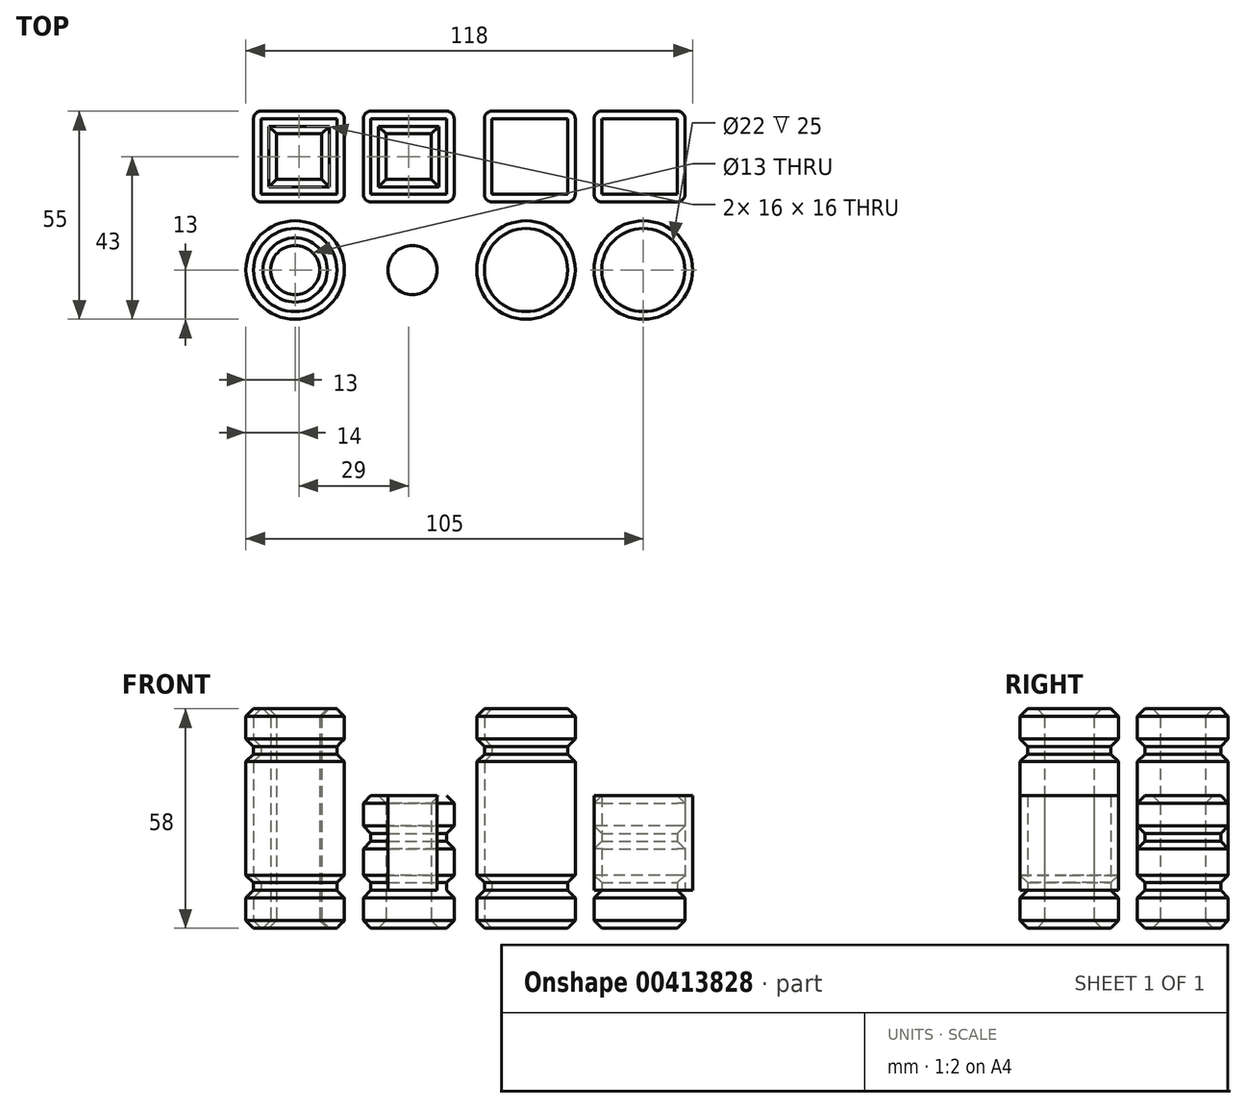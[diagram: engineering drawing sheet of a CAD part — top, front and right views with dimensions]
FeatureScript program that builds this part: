
annotation { "Feature Type Name" : "Feature", "Feature Type Description" : "" }
export const myFeature = defineFeature(function(context is Context, id is Id, definition is map)
    precondition{}
    {
        {
            var Q0;
            Q0=qCreatedBy(makeId("Top.planeOp"),FACE);
            var sketch = newSketch(context, id + "F0", { "sketchPlane" : qUnion([Q0])});
            skCircle(sketch, "E0", {"center": v(-46, -15.5) * mm, "radius": 13 * mm});
            skLineSegment(sketch, "E1.bottom", {"start": v(-35, 2.5) * mm, "end": v(-55, 2.5) * mm});
            skLineSegment(sketch, "E1.top", {"start": v(-35, 26.5) * mm, "end": v(-55, 26.5) * mm});
            skLineSegment(sketch, "E1.left", {"start": v(-33, 4.5) * mm, "end": v(-33, 24.5) * mm});
            skLineSegment(sketch, "E1.right", {"start": v(-57, 4.5) * mm, "end": v(-57, 24.5) * mm});
            skPoint(sketch, "E1.middle", {"position": v(-45, 14.5) * mm});
            skCircle(sketch, "E2.MirrorC", {"center": v(46, -15.5) * mm, "radius": 13 * mm});
            skLineSegment(sketch, "E3.MirrorCS", {"start": v(35, 2.5) * mm, "end": v(55, 2.5) * mm});
            skLineSegment(sketch, "E4.MirrorCS", {"start": v(35, 26.5) * mm, "end": v(55, 26.5) * mm});
            skLineSegment(sketch, "E5.MirrorCS", {"start": v(57, 4.5) * mm, "end": v(57, 24.5) * mm});
            skLineSegment(sketch, "E6.MirrorCS", {"start": v(33, 4.5) * mm, "end": v(33, 24.5) * mm});
            skPoint(sketch, "E7.MirrorP", {"position": v(45, 14.5) * mm});
            skLineSegment(sketch, "E8", {"start": v(-30.5, 50.13) * mm, "end": v(-30.5, -54.87) * mm, "construction": true});
            skLineSegment(sketch, "E9.MirrorCS", {"start": v(30.5, 50.13) * mm, "end": v(30.5, -54.87) * mm, "construction": true});
            skLineSegment(sketch, "E10.MirrorCS", {"start": v(-4, 4.5) * mm, "end": v(-4, 24.5) * mm});
            skLineSegment(sketch, "E11.MirrorCS", {"start": v(-28, 4.5) * mm, "end": v(-28, 24.5) * mm});
            skLineSegment(sketch, "E12.MirrorCS", {"start": v(-26, 26.5) * mm, "end": v(-6, 26.5) * mm});
            skLineSegment(sketch, "E13.MirrorCS", {"start": v(-26, 2.5) * mm, "end": v(-6, 2.5) * mm});
            skPoint(sketch, "E14.MirrorP", {"position": v(-16, 14.5) * mm});
            skCircle(sketch, "E15.MirrorC", {"center": v(-15, -15.5) * mm, "radius": 13 * mm});
            skLineSegment(sketch, "E16.MirrorCS", {"start": v(26, 26.5) * mm, "end": v(6, 26.5) * mm});
            skPoint(sketch, "E17.MirrorP", {"position": v(16, 14.5) * mm});
            skCircle(sketch, "E18.MirrorC", {"center": v(15, -15.5) * mm, "radius": 13 * mm});
            skLineSegment(sketch, "E19.MirrorCS", {"start": v(26, 2.5) * mm, "end": v(6, 2.5) * mm});
            skLineSegment(sketch, "E20.MirrorCS", {"start": v(4, 4.5) * mm, "end": v(4, 24.5) * mm});
            skLineSegment(sketch, "E21.MirrorCS", {"start": v(28, 4.5) * mm, "end": v(28, 24.5) * mm});
            skLineSegment(sketch, "E22.bottom", {"start": v(-39, 8.5) * mm, "end": v(-51, 8.5) * mm});
            skLineSegment(sketch, "E22.top", {"start": v(-39, 20.5) * mm, "end": v(-51, 20.5) * mm});
            skLineSegment(sketch, "E22.left", {"start": v(-39, 8.5) * mm, "end": v(-39, 20.5) * mm});
            skLineSegment(sketch, "E22.right", {"start": v(-51, 8.5) * mm, "end": v(-51, 20.5) * mm});
            skCircle(sketch, "E23", {"center": v(-46, -15.5) * mm, "radius": 6.5 * mm});
            skLineSegment(sketch, "E24.MirrorCS", {"start": v(-22, 20.5) * mm, "end": v(-10, 20.5) * mm});
            skLineSegment(sketch, "E25.MirrorCS", {"start": v(-22, 8.5) * mm, "end": v(-10, 8.5) * mm});
            skLineSegment(sketch, "E26.MirrorCS", {"start": v(-10, 8.5) * mm, "end": v(-10, 20.5) * mm});
            skLineSegment(sketch, "E27.MirrorCS", {"start": v(-22, 8.5) * mm, "end": v(-22, 20.5) * mm});
            skCircle(sketch, "E28.MirrorC", {"center": v(-15, -15.5) * mm, "radius": 6.5 * mm});
            skPoint(sketch, "E29.visualSharp", {"position": v(-57, 26.5) * mm});
            skArc(sketch, "E29.filletArc", {"start": v(-55, 26.5) * mm, "mid": v(-56.41, 25.91) * mm, "end": v(-57, 24.5) * mm});
            skPoint(sketch, "E30.visualSharp", {"position": v(-33, 26.5) * mm});
            skArc(sketch, "E30.filletArc", {"start": v(-33, 24.5) * mm, "mid": v(-33.59, 25.91) * mm, "end": v(-35, 26.5) * mm});
            skPoint(sketch, "E31.visualSharp", {"position": v(-33, 2.5) * mm});
            skArc(sketch, "E31.filletArc", {"start": v(-35, 2.5) * mm, "mid": v(-33.59, 3.09) * mm, "end": v(-33, 4.5) * mm});
            skPoint(sketch, "E32.visualSharp", {"position": v(-57, 2.5) * mm});
            skArc(sketch, "E32.filletArc", {"start": v(-57, 4.5) * mm, "mid": v(-56.41, 3.09) * mm, "end": v(-55, 2.5) * mm});
            skPoint(sketch, "E33.visualSharp", {"position": v(-28, 26.5) * mm});
            skArc(sketch, "E33.filletArc", {"start": v(-26, 26.5) * mm, "mid": v(-27.41, 25.91) * mm, "end": v(-28, 24.5) * mm});
            skPoint(sketch, "E34.visualSharp", {"position": v(-4, 26.5) * mm});
            skArc(sketch, "E34.filletArc", {"start": v(-4, 24.5) * mm, "mid": v(-4.59, 25.91) * mm, "end": v(-6, 26.5) * mm});
            skPoint(sketch, "E35.visualSharp", {"position": v(-4, 2.5) * mm});
            skArc(sketch, "E35.filletArc", {"start": v(-6, 2.5) * mm, "mid": v(-4.59, 3.09) * mm, "end": v(-4, 4.5) * mm});
            skPoint(sketch, "E36.visualSharp", {"position": v(-28, 2.5) * mm});
            skArc(sketch, "E36.filletArc", {"start": v(-28, 4.5) * mm, "mid": v(-27.41, 3.09) * mm, "end": v(-26, 2.5) * mm});
            skPoint(sketch, "E37.visualSharp", {"position": v(4, 26.5) * mm});
            skArc(sketch, "E37.filletArc", {"start": v(6, 26.5) * mm, "mid": v(4.59, 25.91) * mm, "end": v(4, 24.5) * mm});
            skPoint(sketch, "E38.visualSharp", {"position": v(28, 26.5) * mm});
            skArc(sketch, "E38.filletArc", {"start": v(28, 24.5) * mm, "mid": v(27.41, 25.91) * mm, "end": v(26, 26.5) * mm});
            skPoint(sketch, "E39.visualSharp", {"position": v(28, 2.5) * mm});
            skArc(sketch, "E39.filletArc", {"start": v(26, 2.5) * mm, "mid": v(27.41, 3.09) * mm, "end": v(28, 4.5) * mm});
            skPoint(sketch, "E40.visualSharp", {"position": v(4, 2.5) * mm});
            skArc(sketch, "E40.filletArc", {"start": v(4, 4.5) * mm, "mid": v(4.59, 3.09) * mm, "end": v(6, 2.5) * mm});
            skPoint(sketch, "E41.visualSharp", {"position": v(33, 26.5) * mm});
            skArc(sketch, "E41.filletArc", {"start": v(35, 26.5) * mm, "mid": v(33.59, 25.91) * mm, "end": v(33, 24.5) * mm});
            skPoint(sketch, "E42.visualSharp", {"position": v(57, 26.5) * mm});
            skArc(sketch, "E42.filletArc", {"start": v(57, 24.5) * mm, "mid": v(56.41, 25.91) * mm, "end": v(55, 26.5) * mm});
            skPoint(sketch, "E43.visualSharp", {"position": v(57, 2.5) * mm});
            skArc(sketch, "E43.filletArc", {"start": v(55, 2.5) * mm, "mid": v(56.41, 3.09) * mm, "end": v(57, 4.5) * mm});
            skPoint(sketch, "E44.visualSharp", {"position": v(33, 2.5) * mm});
            skArc(sketch, "E44.filletArc", {"start": v(33, 4.5) * mm, "mid": v(33.59, 3.09) * mm, "end": v(35, 2.5) * mm});
            skSolve(sketch);
        }
        {
            var Q0;
            Q0=makeQuery(id+"F0.imprint","IMPRINT",FACE,{"disambiguationData":[TD([[makeQuery(id+"F0.imprint","IMPRINT",EDGE,{"derivedFrom":sQuery(id+"F0.wireOp",EDGE,"E16.MirrorCS")}),1.0]])]});
            var Q1;
            Q1=makeQuery(id+"F0.imprint","IMPRINT",FACE,{"disambiguationData":[TD([[makeQuery(id+"F0.imprint","IMPRINT",EDGE,{"derivedFrom":sQuery(id+"F0.wireOp",EDGE,"E18.MirrorC")}),1.0]])]});
            var Q2;
            Q2=makeQuery(id+"F0.imprint","IMPRINT",FACE,{"disambiguationData":[TD([[makeQuery(id+"F0.imprint","IMPRINT",EDGE,{"derivedFrom":sQuery(id+"F0.wireOp",EDGE,"E0")}),1.0]])]});
            var Q3;
            Q3=makeQuery(id+"F0.imprint","IMPRINT",FACE,{"disambiguationData":[TD([[makeQuery(id+"F0.imprint","IMPRINT",EDGE,{"derivedFrom":sQuery(id+"F0.wireOp",EDGE,"E10.MirrorCS")}),1.0]])]});
            var Q4;
            Q4=makeQuery(id+"F0.imprint","IMPRINT",FACE,{"disambiguationData":[TD([[makeQuery(id+"F0.imprint","IMPRINT",EDGE,{"derivedFrom":sQuery(id+"F0.wireOp",EDGE,"E15.MirrorC")}),-1.0]])]});
            var Q5;
            Q5=makeQuery(id+"F0.imprint","IMPRINT",FACE,{"disambiguationData":[TD([[makeQuery(id+"F0.imprint","IMPRINT",EDGE,{"derivedFrom":sQuery(id+"F0.wireOp",EDGE,"E3.MirrorCS")}),1.0]])]});
            var Q6;
            Q6=makeQuery(id+"F0.imprint","IMPRINT",FACE,{"disambiguationData":[TD([[makeQuery(id+"F0.imprint","IMPRINT",EDGE,{"derivedFrom":sQuery(id+"F0.wireOp",EDGE,"E2.MirrorC")}),-1.0]])]});
            var Q7;
            Q7=makeQuery(id+"F0.imprint","IMPRINT",FACE,{"disambiguationData":[TD([[makeQuery(id+"F0.imprint","IMPRINT",EDGE,{"derivedFrom":sQuery(id+"F0.wireOp",EDGE,"E1.bottom")}),-1.0]])]});
            extrude(context, id + "F1", {"entities" : qUnion([Q0, Q1, Q2, Q3, Q4, Q5, Q6, Q7]), "depth" : 10 * mm});
        }
        {
            var Q0;
            Q0=makeQuery(id+"F1.opExtrude","CAP_FACE",FACE,{"disambiguationData":[OSD([sQuery(id+"F0.wireOp",EDGE,"E18.MirrorC")])],"isStart":false});
            var sketch = newSketch(context, id + "F2", { "sketchPlane" : qUnion([Q0])});
            skCircle(sketch, "E45.0.0", {"center": v(-46, -15.5) * mm, "radius": 13 * mm, "construction": true});
            skCircle(sketch, "E46.0.0", {"center": v(-15, -15.5) * mm, "radius": 13 * mm, "construction": true});
            skCircle(sketch, "E47.0.0", {"center": v(15, -15.5) * mm, "radius": 13 * mm, "construction": true});
            skCircle(sketch, "E48.0.0", {"center": v(46, -15.5) * mm, "radius": 13 * mm, "construction": true});
            skPoint(sketch, "E49.0", {"position": v(-45, 14.5) * mm});
            skPoint(sketch, "E50.0", {"position": v(-16, 14.5) * mm});
            skPoint(sketch, "E51.0", {"position": v(16, 14.5) * mm});
            skPoint(sketch, "E52.0", {"position": v(45, 14.5) * mm});
            skCircle(sketch, "E53.0.0", {"center": v(46, -15.5) * mm, "radius": 13 * mm});
            skLineSegment(sketch, "E54.bottom", {"start": v(-35, 4.5) * mm, "end": v(-55, 4.5) * mm});
            skLineSegment(sketch, "E54.top", {"start": v(-35, 24.5) * mm, "end": v(-55, 24.5) * mm});
            skLineSegment(sketch, "E54.left", {"start": v(-35, 4.5) * mm, "end": v(-35, 24.5) * mm});
            skLineSegment(sketch, "E54.right", {"start": v(-55, 4.5) * mm, "end": v(-55, 24.5) * mm});
            skLineSegment(sketch, "E55.0", {"start": v(-30.5, 50.13) * mm, "end": v(-30.5, -54.87) * mm, "construction": true});
            skLineSegment(sketch, "E56.0", {"start": v(30.5, 50.13) * mm, "end": v(30.5, -54.87) * mm, "construction": true});
            skLineSegment(sketch, "E57.0", {"start": v(-51, 8.5) * mm, "end": v(-51, 20.5) * mm});
            skLineSegment(sketch, "E58.0", {"start": v(-39, 20.5) * mm, "end": v(-51, 20.5) * mm});
            skLineSegment(sketch, "E59.0", {"start": v(-39, 8.5) * mm, "end": v(-39, 20.5) * mm});
            skPoint(sketch, "E60.0", {"position": v(-45, 8.5) * mm});
            skLineSegment(sketch, "E61.0", {"start": v(-39, 8.5) * mm, "end": v(-51, 8.5) * mm});
            skLineSegment(sketch, "E62.0", {"start": v(-22, 8.5) * mm, "end": v(-10, 8.5) * mm});
            skLineSegment(sketch, "E63.0", {"start": v(-22, 8.5) * mm, "end": v(-22, 20.5) * mm});
            skLineSegment(sketch, "E64.0", {"start": v(-22, 20.5) * mm, "end": v(-10, 20.5) * mm});
            skLineSegment(sketch, "E65.0", {"start": v(-10, 8.5) * mm, "end": v(-10, 20.5) * mm});
            skCircle(sketch, "E66.0", {"center": v(-46, -15.5) * mm, "radius": 6.5 * mm});
            skCircle(sketch, "E67.0", {"center": v(-15, -15.5) * mm, "radius": 6.5 * mm});
            skLineSegment(sketch, "E68.MirrorCS", {"start": v(-26, 4.5) * mm, "end": v(-26, 24.5) * mm});
            skLineSegment(sketch, "E69.MirrorCS", {"start": v(-26, 24.5) * mm, "end": v(-6, 24.5) * mm});
            skLineSegment(sketch, "E70.MirrorCS", {"start": v(-6, 4.5) * mm, "end": v(-6, 24.5) * mm});
            skLineSegment(sketch, "E71.MirrorCS", {"start": v(-26, 4.5) * mm, "end": v(-6, 4.5) * mm});
            skCircle(sketch, "E72", {"center": v(-46, -15.5) * mm, "radius": 11 * mm});
            skCircle(sketch, "E73.MirrorC", {"center": v(-15, -15.5) * mm, "radius": 11 * mm});
            skLineSegment(sketch, "E74.MirrorCS", {"start": v(6, 4.5) * mm, "end": v(6, 24.5) * mm});
            skLineSegment(sketch, "E75.MirrorCS", {"start": v(26, 24.5) * mm, "end": v(6, 24.5) * mm});
            skLineSegment(sketch, "E76.MirrorCS", {"start": v(26, 4.5) * mm, "end": v(26, 24.5) * mm});
            skLineSegment(sketch, "E77.MirrorCS", {"start": v(26, 4.5) * mm, "end": v(6, 4.5) * mm});
            skLineSegment(sketch, "E78.MirrorCS", {"start": v(35, 4.5) * mm, "end": v(35, 24.5) * mm});
            skLineSegment(sketch, "E79.MirrorCS", {"start": v(35, 24.5) * mm, "end": v(55, 24.5) * mm});
            skLineSegment(sketch, "E80.MirrorCS", {"start": v(55, 4.5) * mm, "end": v(55, 24.5) * mm});
            skLineSegment(sketch, "E81.MirrorCS", {"start": v(35, 4.5) * mm, "end": v(55, 4.5) * mm});
            skCircle(sketch, "E82.MirrorC", {"center": v(15, -15.5) * mm, "radius": 11 * mm});
            skCircle(sketch, "E83.MirrorC", {"center": v(46, -15.5) * mm, "radius": 11 * mm});
            skSolve(sketch);
        }
        {
            var Q0;
            Q0=makeQuery(id+"F2.imprint","IMPRINT",FACE,{"disambiguationData":[TD([[makeQuery(id+"F2.imprint","IMPRINT",EDGE,{"derivedFrom":sQuery(id+"F2.wireOp",EDGE,"E54.bottom")}),-1.0]])]});
            var Q1;
            Q1=makeQuery(id+"F2.imprint","IMPRINT",FACE,{"disambiguationData":[TD([[makeQuery(id+"F2.imprint","IMPRINT",EDGE,{"derivedFrom":sQuery(id+"F2.wireOp",EDGE,"E66.0")}),-1.0]])]});
            var Q2;
            Q2=makeQuery(id+"F2.imprint","IMPRINT",FACE,{"disambiguationData":[TD([[makeQuery(id+"F2.imprint","IMPRINT",EDGE,{"derivedFrom":sQuery(id+"F2.wireOp",EDGE,"E82.MirrorC")}),1.0]])]});
            var Q3;
            Q3=makeQuery(id+"F2.imprint","IMPRINT",FACE,{"disambiguationData":[TD([[makeQuery(id+"F2.imprint","IMPRINT",EDGE,{"derivedFrom":sQuery(id+"F2.wireOp",EDGE,"E74.MirrorCS")}),-1.0]])]});
            extrude(context, id + "F3", {"entities" : qUnion([Q0, Q1, Q2, Q3]), "operationType" : NewBodyOperationType.ADD, "depth" : 48 * mm});
        }
        {
            var Q0;
            Q0=makeQuery(id+"F2.imprint","IMPRINT",FACE,{"disambiguationData":[TD([[makeQuery(id+"F2.imprint","IMPRINT",EDGE,{"derivedFrom":sQuery(id+"F2.wireOp",EDGE,"E62.0")}),-1.0]])]});
            var Q1;
            Q1=makeQuery(id+"F2.imprint","IMPRINT",FACE,{"disambiguationData":[TD([[makeQuery(id+"F2.imprint","IMPRINT",EDGE,{"derivedFrom":sQuery(id+"F2.wireOp",EDGE,"E67.0")}),1.0]])]});
            var Q2;
            Q2=makeQuery(id+"F2.imprint","IMPRINT",FACE,{"disambiguationData":[TD([[makeQuery(id+"F2.imprint","IMPRINT",EDGE,{"derivedFrom":sQuery(id+"F2.wireOp",EDGE,"E78.MirrorCS")}),-1.0]])]});
            var Q3;
            Q3=makeQuery(id+"F2.imprint","IMPRINT",FACE,{"disambiguationData":[TD([[makeQuery(id+"F2.imprint","IMPRINT",EDGE,{"derivedFrom":sQuery(id+"F2.wireOp",EDGE,"E83.MirrorC")}),-1.0]])]});
            extrude(context, id + "F4", {"entities" : qUnion([Q0, Q1, Q2, Q3]), "operationType" : NewBodyOperationType.ADD, "depth" : 25 * mm});
        }
        {
            var Q0;
            Q0=makeQuery(id+"F0.imprint","IMPRINT",FACE,{"disambiguationData":[TD([[makeQuery(id+"F0.imprint","IMPRINT",EDGE,{"derivedFrom":sQuery(id+"F0.wireOp",EDGE,"E1.bottom")}),-1.0]])]});
            var Q1;
            Q1=makeQuery(id+"F0.imprint","IMPRINT",FACE,{"disambiguationData":[TD([[makeQuery(id+"F0.imprint","IMPRINT",EDGE,{"derivedFrom":sQuery(id+"F0.wireOp",EDGE,"E0")}),1.0]])]});
            var Q2;
            Q2=makeQuery(id+"F0.imprint","IMPRINT",FACE,{"disambiguationData":[TD([[makeQuery(id+"F0.imprint","IMPRINT",EDGE,{"derivedFrom":sQuery(id+"F0.wireOp",EDGE,"E18.MirrorC")}),1.0]])]});
            var Q3;
            Q3=makeQuery(id+"F0.imprint","IMPRINT",FACE,{"disambiguationData":[TD([[makeQuery(id+"F0.imprint","IMPRINT",EDGE,{"derivedFrom":sQuery(id+"F0.wireOp",EDGE,"E16.MirrorCS")}),1.0]])]});
            extrude(context, id + "F5", {"entities" : qUnion([Q0, Q1, Q2, Q3]), "operationType" : NewBodyOperationType.ADD, "depth" : 46 * mm, "hasSecondDirection" : true, "secondDirectionOppositeDirection" : false, "secondDirectionDepth" : 12 * mm});
        }
        {
            var Q0;
            Q0=makeQuery(id+"F0.imprint","IMPRINT",FACE,{"disambiguationData":[TD([[makeQuery(id+"F0.imprint","IMPRINT",EDGE,{"derivedFrom":sQuery(id+"F0.wireOp",EDGE,"E10.MirrorCS")}),1.0]])]});
            var Q1;
            Q1=makeQuery(id+"F0.imprint","IMPRINT",FACE,{"disambiguationData":[TD([[makeQuery(id+"F0.imprint","IMPRINT",EDGE,{"derivedFrom":sQuery(id+"F0.wireOp",EDGE,"E15.MirrorC")}),-1.0]])]});
            var Q2;
            Q2=makeQuery(id+"F0.imprint","IMPRINT",FACE,{"disambiguationData":[TD([[makeQuery(id+"F0.imprint","IMPRINT",EDGE,{"derivedFrom":sQuery(id+"F0.wireOp",EDGE,"E2.MirrorC")}),-1.0]])]});
            var Q3;
            Q3=makeQuery(id+"F0.imprint","IMPRINT",FACE,{"disambiguationData":[TD([[makeQuery(id+"F0.imprint","IMPRINT",EDGE,{"derivedFrom":sQuery(id+"F0.wireOp",EDGE,"E3.MirrorCS")}),1.0]])]});
            extrude(context, id + "F6", {"entities" : qUnion([Q0, Q1, Q2, Q3]), "operationType" : NewBodyOperationType.ADD, "depth" : 23 * mm, "hasSecondDirection" : true, "secondDirectionOppositeDirection" : false, "secondDirectionDepth" : 12 * mm});
        }
        {
            var Q0;
            Q0=makeQuery(id+"F5.opExtrude","CAP_FACE",FACE,{"disambiguationData":[OSD([sQuery(id+"F0.wireOp",EDGE,"E1.bottom"),sQuery(id+"F0.wireOp",EDGE,"E1.top"),sQuery(id+"F0.wireOp",EDGE,"E1.left"),sQuery(id+"F0.wireOp",EDGE,"E1.right"),sQuery(id+"F0.wireOp",EDGE,"E22.bottom"),sQuery(id+"F0.wireOp",EDGE,"E22.top"),sQuery(id+"F0.wireOp",EDGE,"E22.left"),sQuery(id+"F0.wireOp",EDGE,"E22.right")])],"isStart":false});
            var Q1;
            Q1=makeQuery(id+"F5.opExtrude","CAP_FACE",FACE,{"disambiguationData":[OSD([sQuery(id+"F0.wireOp",EDGE,"E0"),sQuery(id+"F0.wireOp",EDGE,"E23")])],"isStart":false});
            var Q2;
            Q2=makeQuery(id+"F6.opExtrude","CAP_FACE",FACE,{"disambiguationData":[OSD([sQuery(id+"F0.wireOp",EDGE,"E10.MirrorCS"),sQuery(id+"F0.wireOp",EDGE,"E11.MirrorCS"),sQuery(id+"F0.wireOp",EDGE,"E12.MirrorCS"),sQuery(id+"F0.wireOp",EDGE,"E13.MirrorCS"),sQuery(id+"F0.wireOp",EDGE,"E24.MirrorCS"),sQuery(id+"F0.wireOp",EDGE,"E25.MirrorCS"),sQuery(id+"F0.wireOp",EDGE,"E26.MirrorCS"),sQuery(id+"F0.wireOp",EDGE,"E27.MirrorCS")])],"isStart":false});
            var Q3;
            Q3=makeQuery(id+"F6.opExtrude","CAP_FACE",FACE,{"disambiguationData":[OSD([sQuery(id+"F0.wireOp",EDGE,"E15.MirrorC"),sQuery(id+"F0.wireOp",EDGE,"E28.MirrorC")])],"isStart":false});
            var Q4;
            Q4=makeQuery(id+"F5.opExtrude","CAP_FACE",FACE,{"disambiguationData":[OSD([sQuery(id+"F0.wireOp",EDGE,"E16.MirrorCS"),sQuery(id+"F0.wireOp",EDGE,"E19.MirrorCS"),sQuery(id+"F0.wireOp",EDGE,"E20.MirrorCS"),sQuery(id+"F0.wireOp",EDGE,"E21.MirrorCS")])],"isStart":false});
            var Q5;
            Q5=makeQuery(id+"F5.opExtrude","CAP_FACE",FACE,{"disambiguationData":[OSD([sQuery(id+"F0.wireOp",EDGE,"E18.MirrorC")])],"isStart":false});
            var Q6;
            Q6=makeQuery(id+"F6.opExtrude","CAP_FACE",FACE,{"disambiguationData":[OSD([sQuery(id+"F0.wireOp",EDGE,"E3.MirrorCS"),sQuery(id+"F0.wireOp",EDGE,"E4.MirrorCS"),sQuery(id+"F0.wireOp",EDGE,"E5.MirrorCS"),sQuery(id+"F0.wireOp",EDGE,"E6.MirrorCS")])],"isStart":false});
            var Q7;
            Q7=makeQuery(id+"F6.opExtrude","CAP_FACE",FACE,{"disambiguationData":[OSD([sQuery(id+"F0.wireOp",EDGE,"E2.MirrorC")])],"isStart":false});
            extrude(context, id + "F7", {"entities" : qUnion([Q0, Q1, Q2, Q3, Q4, Q5, Q6, Q7]), "operationType" : NewBodyOperationType.ADD, "depth" : 12 * mm, "hasSecondDirection" : true, "secondDirectionOppositeDirection" : false, "secondDirectionDepth" : 2 * mm});
        }
        {
            var Q0;
            Q0=makeQuery(id+"F1.opExtrude","CAP_EDGE",EDGE,{"disambiguationData":[OSD([sQuery(id+"F0.wireOp",EDGE,"E1.top")])],"isStart":true});
            var Q1;
            Q1=makeQuery(id+"F1.opExtrude","CAP_EDGE",EDGE,{"disambiguationData":[OSD([sQuery(id+"F0.wireOp",EDGE,"E1.right")])],"isStart":true});
            var Q2;
            Q2=makeQuery(id+"F1.opExtrude","CAP_EDGE",EDGE,{"disambiguationData":[OSD([sQuery(id+"F0.wireOp",EDGE,"E1.bottom")])],"isStart":true});
            var Q3;
            Q3=makeQuery(id+"F1.opExtrude","CAP_EDGE",EDGE,{"disambiguationData":[OSD([sQuery(id+"F0.wireOp",EDGE,"E1.left")])],"isStart":true});
            var Q4;
            Q4=makeQuery(id+"F1.opExtrude","CAP_EDGE",EDGE,{"disambiguationData":[OSD([sQuery(id+"F0.wireOp",EDGE,"E22.left")])],"isStart":true});
            var Q5;
            Q5=makeQuery(id+"F1.opExtrude","CAP_EDGE",EDGE,{"disambiguationData":[OSD([sQuery(id+"F0.wireOp",EDGE,"E22.bottom")])],"isStart":true});
            var Q6;
            Q6=makeQuery(id+"F1.opExtrude","CAP_EDGE",EDGE,{"disambiguationData":[OSD([sQuery(id+"F0.wireOp",EDGE,"E22.right")])],"isStart":true});
            var Q7;
            Q7=makeQuery(id+"F1.opExtrude","CAP_EDGE",EDGE,{"disambiguationData":[OSD([sQuery(id+"F0.wireOp",EDGE,"E22.top")])],"isStart":true});
            var Q8;
            Q8=makeQuery(id+"F1.opExtrude","CAP_EDGE",EDGE,{"disambiguationData":[OSD([sQuery(id+"F0.wireOp",EDGE,"E1.right")])],"isStart":false});
            var Q9;
            Q9=makeQuery(id+"F1.opExtrude","CAP_EDGE",EDGE,{"disambiguationData":[OSD([sQuery(id+"F0.wireOp",EDGE,"E1.top")])],"isStart":false});
            var Q10;
            Q10=makeQuery(id+"F5.opExtrude","CAP_EDGE",EDGE,{"disambiguationData":[OSD([sQuery(id+"F0.wireOp",EDGE,"E1.top")])],"isStart":true});
            var Q11;
            Q11=makeQuery(id+"F5.opExtrude","CAP_EDGE",EDGE,{"disambiguationData":[OSD([sQuery(id+"F0.wireOp",EDGE,"E1.right")])],"isStart":true});
            var Q12;
            Q12=makeQuery(id+"F1.opExtrude","CAP_EDGE",EDGE,{"disambiguationData":[OSD([sQuery(id+"F0.wireOp",EDGE,"E1.bottom")])],"isStart":false});
            var Q13;
            Q13=makeQuery(id+"F5.opExtrude","CAP_EDGE",EDGE,{"disambiguationData":[OSD([sQuery(id+"F0.wireOp",EDGE,"E1.bottom")])],"isStart":true});
            var Q14;
            Q14=makeQuery(id+"F1.opExtrude","CAP_EDGE",EDGE,{"disambiguationData":[OSD([sQuery(id+"F0.wireOp",EDGE,"E1.left")])],"isStart":false});
            var Q15;
            Q15=makeQuery(id+"F5.opExtrude","CAP_EDGE",EDGE,{"disambiguationData":[OSD([sQuery(id+"F0.wireOp",EDGE,"E1.left")])],"isStart":true});
            var Q16;
            Q16=makeQuery(id+"F5.opExtrude","CAP_EDGE",EDGE,{"disambiguationData":[OSD([sQuery(id+"F0.wireOp",EDGE,"E1.right")])],"isStart":false});
            var Q17;
            Q17=makeQuery(id+"F7.opExtrude","CAP_EDGE",EDGE,{"disambiguationData":[OSD([sQuery(id+"F0.wireOp",EDGE,"E1.right")])],"isStart":true});
            var Q18;
            Q18=makeQuery(id+"F5.opExtrude","CAP_EDGE",EDGE,{"disambiguationData":[OSD([sQuery(id+"F0.wireOp",EDGE,"E1.bottom")])],"isStart":false});
            var Q19;
            Q19=makeQuery(id+"F7.opExtrude","CAP_EDGE",EDGE,{"disambiguationData":[OSD([sQuery(id+"F0.wireOp",EDGE,"E1.bottom")])],"isStart":true});
            var Q20;
            Q20=makeQuery(id+"F5.opExtrude","CAP_EDGE",EDGE,{"disambiguationData":[OSD([sQuery(id+"F0.wireOp",EDGE,"E1.top")])],"isStart":false});
            var Q21;
            Q21=makeQuery(id+"F7.opExtrude","CAP_EDGE",EDGE,{"disambiguationData":[OSD([sQuery(id+"F0.wireOp",EDGE,"E1.top")])],"isStart":true});
            var Q22;
            Q22=makeQuery(id+"F5.opExtrude","CAP_EDGE",EDGE,{"disambiguationData":[OSD([sQuery(id+"F0.wireOp",EDGE,"E1.left")])],"isStart":false});
            var Q23;
            Q23=makeQuery(id+"F7.opExtrude","CAP_EDGE",EDGE,{"disambiguationData":[OSD([sQuery(id+"F0.wireOp",EDGE,"E1.left")])],"isStart":true});
            var Q24;
            Q24=makeQuery(id+"F7.boolean.opBoolean","MERGE",FACE,{"derivedFrom":[makeQuery(id+"F3.opExtrude","CAP_FACE",FACE,{"disambiguationData":[OSD([sQuery(id+"F2.wireOp",EDGE,"E54.bottom"),sQuery(id+"F2.wireOp",EDGE,"E54.top"),sQuery(id+"F2.wireOp",EDGE,"E54.left"),sQuery(id+"F2.wireOp",EDGE,"E54.right"),sQuery(id+"F2.wireOp",EDGE,"E57.0"),sQuery(id+"F2.wireOp",EDGE,"E58.0"),sQuery(id+"F2.wireOp",EDGE,"E59.0"),sQuery(id+"F2.wireOp",EDGE,"E61.0")])],"isStart":false}),makeQuery(id+"F7.opExtrude","CAP_FACE",FACE,{"disambiguationData":[OSD([sQuery(id+"F0.wireOp",EDGE,"E1.bottom"),sQuery(id+"F0.wireOp",EDGE,"E1.top"),sQuery(id+"F0.wireOp",EDGE,"E1.left"),sQuery(id+"F0.wireOp",EDGE,"E1.right"),sQuery(id+"F0.wireOp",EDGE,"E22.bottom"),sQuery(id+"F0.wireOp",EDGE,"E22.top"),sQuery(id+"F0.wireOp",EDGE,"E22.left"),sQuery(id+"F0.wireOp",EDGE,"E22.right")])],"isStart":false})]});
            var Q25;
            Q25=makeQuery(id+"F1.opExtrude","CAP_FACE",FACE,{"disambiguationData":[OSD([sQuery(id+"F0.wireOp",EDGE,"E0"),sQuery(id+"F0.wireOp",EDGE,"E23")])],"isStart":true});
            var Q26;
            Q26=makeQuery(id+"F1.opExtrude","CAP_EDGE",EDGE,{"disambiguationData":[OSD([sQuery(id+"F0.wireOp",EDGE,"E0")])],"isStart":false});
            var Q27;
            Q27=makeQuery(id+"F5.opExtrude","CAP_EDGE",EDGE,{"disambiguationData":[OSD([sQuery(id+"F0.wireOp",EDGE,"E0")])],"isStart":true});
            var Q28;
            Q28=makeQuery(id+"F5.opExtrude","CAP_EDGE",EDGE,{"disambiguationData":[OSD([sQuery(id+"F0.wireOp",EDGE,"E0")])],"isStart":false});
            var Q29;
            Q29=makeQuery(id+"F7.opExtrude","CAP_EDGE",EDGE,{"disambiguationData":[OSD([sQuery(id+"F0.wireOp",EDGE,"E0")])],"isStart":true});
            var Q30;
            Q30=makeQuery(id+"F7.boolean.opBoolean","MERGE",FACE,{"derivedFrom":[makeQuery(id+"F3.opExtrude","CAP_FACE",FACE,{"disambiguationData":[OSD([sQuery(id+"F2.wireOp",EDGE,"E66.0"),sQuery(id+"F2.wireOp",EDGE,"E72")])],"isStart":false}),makeQuery(id+"F7.opExtrude","CAP_FACE",FACE,{"disambiguationData":[OSD([sQuery(id+"F0.wireOp",EDGE,"E0"),sQuery(id+"F0.wireOp",EDGE,"E23")])],"isStart":false})]});
            var Q31;
            Q31=makeQuery(id+"F1.opExtrude","CAP_FACE",FACE,{"disambiguationData":[OSD([sQuery(id+"F0.wireOp",EDGE,"E10.MirrorCS"),sQuery(id+"F0.wireOp",EDGE,"E11.MirrorCS"),sQuery(id+"F0.wireOp",EDGE,"E12.MirrorCS"),sQuery(id+"F0.wireOp",EDGE,"E13.MirrorCS"),sQuery(id+"F0.wireOp",EDGE,"E24.MirrorCS"),sQuery(id+"F0.wireOp",EDGE,"E25.MirrorCS"),sQuery(id+"F0.wireOp",EDGE,"E26.MirrorCS"),sQuery(id+"F0.wireOp",EDGE,"E27.MirrorCS")])],"isStart":true});
            var Q32;
            Q32=makeQuery(id+"F1.opExtrude","CAP_EDGE",EDGE,{"disambiguationData":[OSD([sQuery(id+"F0.wireOp",EDGE,"E13.MirrorCS")])],"isStart":false});
            var Q33;
            Q33=makeQuery(id+"F6.opExtrude","CAP_EDGE",EDGE,{"disambiguationData":[OSD([sQuery(id+"F0.wireOp",EDGE,"E13.MirrorCS")])],"isStart":true});
            var Q34;
            Q34=makeQuery(id+"F1.opExtrude","CAP_EDGE",EDGE,{"disambiguationData":[OSD([sQuery(id+"F0.wireOp",EDGE,"E11.MirrorCS")])],"isStart":false});
            var Q35;
            Q35=makeQuery(id+"F6.opExtrude","CAP_EDGE",EDGE,{"disambiguationData":[OSD([sQuery(id+"F0.wireOp",EDGE,"E11.MirrorCS")])],"isStart":true});
            var Q36;
            Q36=makeQuery(id+"F6.opExtrude","CAP_EDGE",EDGE,{"disambiguationData":[OSD([sQuery(id+"F0.wireOp",EDGE,"E10.MirrorCS")])],"isStart":true});
            var Q37;
            Q37=makeQuery(id+"F1.opExtrude","CAP_EDGE",EDGE,{"disambiguationData":[OSD([sQuery(id+"F0.wireOp",EDGE,"E10.MirrorCS")])],"isStart":false});
            var Q38;
            Q38=makeQuery(id+"F6.opExtrude","CAP_EDGE",EDGE,{"disambiguationData":[OSD([sQuery(id+"F0.wireOp",EDGE,"E12.MirrorCS")])],"isStart":true});
            var Q39;
            Q39=makeQuery(id+"F1.opExtrude","CAP_EDGE",EDGE,{"disambiguationData":[OSD([sQuery(id+"F0.wireOp",EDGE,"E12.MirrorCS")])],"isStart":false});
            var Q40;
            Q40=makeQuery(id+"F6.opExtrude","CAP_EDGE",EDGE,{"disambiguationData":[OSD([sQuery(id+"F0.wireOp",EDGE,"E12.MirrorCS")])],"isStart":false});
            var Q41;
            Q41=makeQuery(id+"F7.opExtrude","CAP_EDGE",EDGE,{"disambiguationData":[OSD([sQuery(id+"F0.wireOp",EDGE,"E12.MirrorCS")])],"isStart":true});
            var Q42;
            Q42=makeQuery(id+"F7.opExtrude","CAP_EDGE",EDGE,{"disambiguationData":[OSD([sQuery(id+"F0.wireOp",EDGE,"E10.MirrorCS")])],"isStart":true});
            var Q43;
            Q43=makeQuery(id+"F6.opExtrude","CAP_EDGE",EDGE,{"disambiguationData":[OSD([sQuery(id+"F0.wireOp",EDGE,"E10.MirrorCS")])],"isStart":false});
            var Q44;
            Q44=makeQuery(id+"F7.opExtrude","CAP_EDGE",EDGE,{"disambiguationData":[OSD([sQuery(id+"F0.wireOp",EDGE,"E13.MirrorCS")])],"isStart":true});
            var Q45;
            Q45=makeQuery(id+"F6.opExtrude","CAP_EDGE",EDGE,{"disambiguationData":[OSD([sQuery(id+"F0.wireOp",EDGE,"E13.MirrorCS")])],"isStart":false});
            var Q46;
            Q46=makeQuery(id+"F7.opExtrude","CAP_EDGE",EDGE,{"disambiguationData":[OSD([sQuery(id+"F0.wireOp",EDGE,"E11.MirrorCS")])],"isStart":true});
            var Q47;
            Q47=makeQuery(id+"F6.opExtrude","CAP_EDGE",EDGE,{"disambiguationData":[OSD([sQuery(id+"F0.wireOp",EDGE,"E11.MirrorCS")])],"isStart":false});
            var Q48;
            Q48=makeQuery(id+"F7.boolean.opBoolean","MERGE",FACE,{"derivedFrom":[makeQuery(id+"F4.opExtrude","CAP_FACE",FACE,{"disambiguationData":[OSD([sQuery(id+"F2.wireOp",EDGE,"E62.0"),sQuery(id+"F2.wireOp",EDGE,"E63.0"),sQuery(id+"F2.wireOp",EDGE,"E64.0"),sQuery(id+"F2.wireOp",EDGE,"E65.0"),sQuery(id+"F2.wireOp",EDGE,"E68.MirrorCS"),sQuery(id+"F2.wireOp",EDGE,"E69.MirrorCS"),sQuery(id+"F2.wireOp",EDGE,"E70.MirrorCS"),sQuery(id+"F2.wireOp",EDGE,"E71.MirrorCS")])],"isStart":false}),makeQuery(id+"F7.opExtrude","CAP_FACE",FACE,{"disambiguationData":[OSD([sQuery(id+"F0.wireOp",EDGE,"E10.MirrorCS"),sQuery(id+"F0.wireOp",EDGE,"E11.MirrorCS"),sQuery(id+"F0.wireOp",EDGE,"E12.MirrorCS"),sQuery(id+"F0.wireOp",EDGE,"E13.MirrorCS"),sQuery(id+"F0.wireOp",EDGE,"E24.MirrorCS"),sQuery(id+"F0.wireOp",EDGE,"E25.MirrorCS"),sQuery(id+"F0.wireOp",EDGE,"E26.MirrorCS"),sQuery(id+"F0.wireOp",EDGE,"E27.MirrorCS")])],"isStart":false})]});
            var Q49;
            Q49=makeQuery(id+"F1.opExtrude","CAP_FACE",FACE,{"disambiguationData":[OSD([sQuery(id+"F0.wireOp",EDGE,"E15.MirrorC"),sQuery(id+"F0.wireOp",EDGE,"E28.MirrorC")])],"isStart":true});
            var Q50;
            Q50=makeQuery(id+"F1.opExtrude","CAP_EDGE",EDGE,{"disambiguationData":[OSD([sQuery(id+"F0.wireOp",EDGE,"E15.MirrorC")])],"isStart":false});
            var Q51;
            Q51=makeQuery(id+"F6.opExtrude","CAP_EDGE",EDGE,{"disambiguationData":[OSD([sQuery(id+"F0.wireOp",EDGE,"E15.MirrorC")])],"isStart":true});
            var Q52;
            Q52=makeQuery(id+"F6.opExtrude","CAP_EDGE",EDGE,{"disambiguationData":[OSD([sQuery(id+"F0.wireOp",EDGE,"E15.MirrorC")])],"isStart":false});
            var Q53;
            Q53=makeQuery(id+"F7.opExtrude","CAP_EDGE",EDGE,{"disambiguationData":[OSD([sQuery(id+"F0.wireOp",EDGE,"E15.MirrorC")])],"isStart":true});
            var Q54;
            Q54=makeQuery(id+"F7.boolean.opBoolean","MERGE",FACE,{"derivedFrom":[makeQuery(id+"F4.opExtrude","CAP_FACE",FACE,{"disambiguationData":[OSD([sQuery(id+"F2.wireOp",EDGE,"E67.0"),sQuery(id+"F2.wireOp",EDGE,"E73.MirrorC")])],"isStart":false}),makeQuery(id+"F7.opExtrude","CAP_FACE",FACE,{"disambiguationData":[OSD([sQuery(id+"F0.wireOp",EDGE,"E15.MirrorC"),sQuery(id+"F0.wireOp",EDGE,"E28.MirrorC")])],"isStart":false})]});
            var Q55;
            Q55=makeQuery(id+"F1.opExtrude","CAP_FACE",FACE,{"disambiguationData":[OSD([sQuery(id+"F0.wireOp",EDGE,"E16.MirrorCS"),sQuery(id+"F0.wireOp",EDGE,"E19.MirrorCS"),sQuery(id+"F0.wireOp",EDGE,"E20.MirrorCS"),sQuery(id+"F0.wireOp",EDGE,"E21.MirrorCS")])],"isStart":true});
            var Q56;
            Q56=makeQuery(id+"F1.opExtrude","CAP_EDGE",EDGE,{"disambiguationData":[OSD([sQuery(id+"F0.wireOp",EDGE,"E16.MirrorCS")])],"isStart":false});
            var Q57;
            Q57=makeQuery(id+"F1.opExtrude","CAP_EDGE",EDGE,{"disambiguationData":[OSD([sQuery(id+"F0.wireOp",EDGE,"E21.MirrorCS")])],"isStart":false});
            var Q58;
            Q58=makeQuery(id+"F5.opExtrude","CAP_EDGE",EDGE,{"disambiguationData":[OSD([sQuery(id+"F0.wireOp",EDGE,"E16.MirrorCS")])],"isStart":true});
            var Q59;
            Q59=makeQuery(id+"F5.opExtrude","CAP_EDGE",EDGE,{"disambiguationData":[OSD([sQuery(id+"F0.wireOp",EDGE,"E21.MirrorCS")])],"isStart":true});
            var Q60;
            Q60=makeQuery(id+"F1.opExtrude","CAP_EDGE",EDGE,{"disambiguationData":[OSD([sQuery(id+"F0.wireOp",EDGE,"E20.MirrorCS")])],"isStart":false});
            var Q61;
            Q61=makeQuery(id+"F5.opExtrude","CAP_EDGE",EDGE,{"disambiguationData":[OSD([sQuery(id+"F0.wireOp",EDGE,"E20.MirrorCS")])],"isStart":true});
            var Q62;
            Q62=makeQuery(id+"F1.opExtrude","CAP_EDGE",EDGE,{"disambiguationData":[OSD([sQuery(id+"F0.wireOp",EDGE,"E19.MirrorCS")])],"isStart":false});
            var Q63;
            Q63=makeQuery(id+"F5.opExtrude","CAP_EDGE",EDGE,{"disambiguationData":[OSD([sQuery(id+"F0.wireOp",EDGE,"E19.MirrorCS")])],"isStart":true});
            var Q64;
            Q64=makeQuery(id+"F5.opExtrude","CAP_EDGE",EDGE,{"disambiguationData":[OSD([sQuery(id+"F0.wireOp",EDGE,"E20.MirrorCS")])],"isStart":false});
            var Q65;
            Q65=makeQuery(id+"F7.opExtrude","CAP_EDGE",EDGE,{"disambiguationData":[OSD([sQuery(id+"F0.wireOp",EDGE,"E20.MirrorCS")])],"isStart":true});
            var Q66;
            Q66=makeQuery(id+"F7.opExtrude","CAP_EDGE",EDGE,{"disambiguationData":[OSD([sQuery(id+"F0.wireOp",EDGE,"E19.MirrorCS")])],"isStart":true});
            var Q67;
            Q67=makeQuery(id+"F5.opExtrude","CAP_EDGE",EDGE,{"disambiguationData":[OSD([sQuery(id+"F0.wireOp",EDGE,"E19.MirrorCS")])],"isStart":false});
            var Q68;
            Q68=makeQuery(id+"F5.opExtrude","CAP_EDGE",EDGE,{"disambiguationData":[OSD([sQuery(id+"F0.wireOp",EDGE,"E16.MirrorCS")])],"isStart":false});
            var Q69;
            Q69=makeQuery(id+"F7.opExtrude","CAP_EDGE",EDGE,{"disambiguationData":[OSD([sQuery(id+"F0.wireOp",EDGE,"E16.MirrorCS")])],"isStart":true});
            var Q70;
            Q70=makeQuery(id+"F5.opExtrude","CAP_EDGE",EDGE,{"disambiguationData":[OSD([sQuery(id+"F0.wireOp",EDGE,"E21.MirrorCS")])],"isStart":false});
            var Q71;
            Q71=makeQuery(id+"F7.opExtrude","CAP_EDGE",EDGE,{"disambiguationData":[OSD([sQuery(id+"F0.wireOp",EDGE,"E21.MirrorCS")])],"isStart":true});
            var Q72;
            Q72=makeQuery(id+"F7.boolean.opBoolean","MERGE",FACE,{"derivedFrom":[makeQuery(id+"F3.opExtrude","CAP_FACE",FACE,{"disambiguationData":[OSD([sQuery(id+"F2.wireOp",EDGE,"E74.MirrorCS"),sQuery(id+"F2.wireOp",EDGE,"E75.MirrorCS"),sQuery(id+"F2.wireOp",EDGE,"E76.MirrorCS"),sQuery(id+"F2.wireOp",EDGE,"E77.MirrorCS")])],"isStart":false}),makeQuery(id+"F7.opExtrude","CAP_FACE",FACE,{"disambiguationData":[OSD([sQuery(id+"F0.wireOp",EDGE,"E16.MirrorCS"),sQuery(id+"F0.wireOp",EDGE,"E19.MirrorCS"),sQuery(id+"F0.wireOp",EDGE,"E20.MirrorCS"),sQuery(id+"F0.wireOp",EDGE,"E21.MirrorCS")])],"isStart":false})]});
            var Q73;
            Q73=makeQuery(id+"F1.opExtrude","CAP_FACE",FACE,{"disambiguationData":[OSD([sQuery(id+"F0.wireOp",EDGE,"E18.MirrorC")])],"isStart":true});
            var Q74;
            Q74=makeQuery(id+"F1.opExtrude","SWEPT_FACE",FACE,{"disambiguationData":[OSD([sQuery(id+"F0.wireOp",EDGE,"E18.MirrorC")])]});
            var Q75;
            Q75=makeQuery(id+"F5.opExtrude","CAP_EDGE",EDGE,{"disambiguationData":[OSD([sQuery(id+"F0.wireOp",EDGE,"E18.MirrorC")])],"isStart":true});
            var Q76;
            Q76=makeQuery(id+"F5.opExtrude","CAP_EDGE",EDGE,{"disambiguationData":[OSD([sQuery(id+"F0.wireOp",EDGE,"E18.MirrorC")])],"isStart":false});
            var Q77;
            Q77=makeQuery(id+"F7.opExtrude","CAP_EDGE",EDGE,{"disambiguationData":[OSD([sQuery(id+"F0.wireOp",EDGE,"E18.MirrorC")])],"isStart":true});
            var Q78;
            Q78=makeQuery(id+"F7.boolean.opBoolean","MERGE",FACE,{"derivedFrom":[makeQuery(id+"F3.opExtrude","CAP_FACE",FACE,{"disambiguationData":[OSD([sQuery(id+"F2.wireOp",EDGE,"E82.MirrorC")])],"isStart":false}),makeQuery(id+"F7.opExtrude","CAP_FACE",FACE,{"disambiguationData":[OSD([sQuery(id+"F0.wireOp",EDGE,"E18.MirrorC")])],"isStart":false})]});
            var Q79;
            Q79=makeQuery(id+"F1.opExtrude","CAP_FACE",FACE,{"disambiguationData":[OSD([sQuery(id+"F0.wireOp",EDGE,"E3.MirrorCS"),sQuery(id+"F0.wireOp",EDGE,"E4.MirrorCS"),sQuery(id+"F0.wireOp",EDGE,"E5.MirrorCS"),sQuery(id+"F0.wireOp",EDGE,"E6.MirrorCS")])],"isStart":true});
            var Q80;
            Q80=makeQuery(id+"F1.opExtrude","CAP_EDGE",EDGE,{"disambiguationData":[OSD([sQuery(id+"F0.wireOp",EDGE,"E4.MirrorCS")])],"isStart":false});
            var Q81;
            Q81=makeQuery(id+"F6.opExtrude","CAP_EDGE",EDGE,{"disambiguationData":[OSD([sQuery(id+"F0.wireOp",EDGE,"E4.MirrorCS")])],"isStart":true});
            var Q82;
            Q82=makeQuery(id+"F1.opExtrude","CAP_EDGE",EDGE,{"disambiguationData":[OSD([sQuery(id+"F0.wireOp",EDGE,"E5.MirrorCS")])],"isStart":false});
            var Q83;
            Q83=makeQuery(id+"F6.opExtrude","CAP_EDGE",EDGE,{"disambiguationData":[OSD([sQuery(id+"F0.wireOp",EDGE,"E5.MirrorCS")])],"isStart":true});
            var Q84;
            Q84=makeQuery(id+"F1.opExtrude","CAP_EDGE",EDGE,{"disambiguationData":[OSD([sQuery(id+"F0.wireOp",EDGE,"E6.MirrorCS")])],"isStart":false});
            var Q85;
            Q85=makeQuery(id+"F6.opExtrude","CAP_EDGE",EDGE,{"disambiguationData":[OSD([sQuery(id+"F0.wireOp",EDGE,"E6.MirrorCS")])],"isStart":true});
            var Q86;
            Q86=makeQuery(id+"F6.opExtrude","CAP_EDGE",EDGE,{"disambiguationData":[OSD([sQuery(id+"F0.wireOp",EDGE,"E3.MirrorCS")])],"isStart":true});
            var Q87;
            Q87=makeQuery(id+"F1.opExtrude","CAP_EDGE",EDGE,{"disambiguationData":[OSD([sQuery(id+"F0.wireOp",EDGE,"E3.MirrorCS")])],"isStart":false});
            var Q88;
            Q88=makeQuery(id+"F7.opExtrude","CAP_EDGE",EDGE,{"disambiguationData":[OSD([sQuery(id+"F0.wireOp",EDGE,"E3.MirrorCS")])],"isStart":true});
            var Q89;
            Q89=makeQuery(id+"F6.opExtrude","CAP_EDGE",EDGE,{"disambiguationData":[OSD([sQuery(id+"F0.wireOp",EDGE,"E3.MirrorCS")])],"isStart":false});
            var Q90;
            Q90=makeQuery(id+"F7.opExtrude","CAP_EDGE",EDGE,{"disambiguationData":[OSD([sQuery(id+"F0.wireOp",EDGE,"E5.MirrorCS")])],"isStart":true});
            var Q91;
            Q91=makeQuery(id+"F6.opExtrude","CAP_EDGE",EDGE,{"disambiguationData":[OSD([sQuery(id+"F0.wireOp",EDGE,"E5.MirrorCS")])],"isStart":false});
            var Q92;
            Q92=makeQuery(id+"F7.opExtrude","CAP_EDGE",EDGE,{"disambiguationData":[OSD([sQuery(id+"F0.wireOp",EDGE,"E4.MirrorCS")])],"isStart":true});
            var Q93;
            Q93=makeQuery(id+"F6.opExtrude","CAP_EDGE",EDGE,{"disambiguationData":[OSD([sQuery(id+"F0.wireOp",EDGE,"E4.MirrorCS")])],"isStart":false});
            var Q94;
            Q94=makeQuery(id+"F6.opExtrude","CAP_EDGE",EDGE,{"disambiguationData":[OSD([sQuery(id+"F0.wireOp",EDGE,"E6.MirrorCS")])],"isStart":false});
            var Q95;
            Q95=makeQuery(id+"F7.opExtrude","CAP_EDGE",EDGE,{"disambiguationData":[OSD([sQuery(id+"F0.wireOp",EDGE,"E6.MirrorCS")])],"isStart":true});
            var Q96;
            Q96=makeQuery(id+"F7.boolean.opBoolean","MERGE",FACE,{"derivedFrom":[makeQuery(id+"F4.opExtrude","CAP_FACE",FACE,{"disambiguationData":[OSD([sQuery(id+"F2.wireOp",EDGE,"E78.MirrorCS"),sQuery(id+"F2.wireOp",EDGE,"E79.MirrorCS"),sQuery(id+"F2.wireOp",EDGE,"E80.MirrorCS"),sQuery(id+"F2.wireOp",EDGE,"E81.MirrorCS")])],"isStart":false}),makeQuery(id+"F7.opExtrude","CAP_FACE",FACE,{"disambiguationData":[OSD([sQuery(id+"F0.wireOp",EDGE,"E3.MirrorCS"),sQuery(id+"F0.wireOp",EDGE,"E4.MirrorCS"),sQuery(id+"F0.wireOp",EDGE,"E5.MirrorCS"),sQuery(id+"F0.wireOp",EDGE,"E6.MirrorCS")])],"isStart":false})]});
            var Q97;
            Q97=makeQuery(id+"F1.opExtrude","CAP_FACE",FACE,{"disambiguationData":[OSD([sQuery(id+"F0.wireOp",EDGE,"E2.MirrorC")])],"isStart":true});
            var Q98;
            Q98=makeQuery(id+"F1.opExtrude","CAP_EDGE",EDGE,{"disambiguationData":[OSD([sQuery(id+"F0.wireOp",EDGE,"E2.MirrorC")])],"isStart":false});
            var Q99;
            Q99=makeQuery(id+"F6.opExtrude","CAP_EDGE",EDGE,{"disambiguationData":[OSD([sQuery(id+"F0.wireOp",EDGE,"E2.MirrorC")])],"isStart":true});
            var Q100;
            Q100=makeQuery(id+"F6.opExtrude","CAP_EDGE",EDGE,{"disambiguationData":[OSD([sQuery(id+"F0.wireOp",EDGE,"E2.MirrorC")])],"isStart":false});
            var Q101;
            Q101=makeQuery(id+"F7.opExtrude","CAP_EDGE",EDGE,{"disambiguationData":[OSD([sQuery(id+"F0.wireOp",EDGE,"E2.MirrorC")])],"isStart":true});
            var Q102;
            Q102=makeQuery(id+"F7.opExtrude","CAP_EDGE",EDGE,{"disambiguationData":[OSD([sQuery(id+"F0.wireOp",EDGE,"E2.MirrorC")])],"isStart":false});
            chamfer(context, id + "F8", {"entities" : qUnion([Q0, Q1, Q2, Q3, Q4, Q5, Q6, Q7, Q8, Q9, Q10, Q11, Q12, Q13, Q14, Q15, Q16, Q17, Q18, Q19, Q20, Q21, Q22, Q23, Q24, Q25, Q26, Q27, Q28, Q29, Q30, Q31, Q32, Q33, Q34, Q35, Q36, Q37, Q38, Q39, Q40, Q41, Q42, Q43, Q44, Q45, Q46, Q47, Q48, Q49, Q50, Q51, Q52, Q53, Q54, Q55, Q56, Q57, Q58, Q59, Q60, Q61, Q62, Q63, Q64, Q65, Q66, Q67, Q68, Q69, Q70, Q71, Q72, Q73, Q74, Q75, Q76, Q77, Q78, Q79, Q80, Q81, Q82, Q83, Q84, Q85, Q86, Q87, Q88, Q89, Q90, Q91, Q92, Q93, Q94, Q95, Q96, Q97, Q98, Q99, Q100, Q101, Q102]), "width" : 2 * mm});
        }
    });
